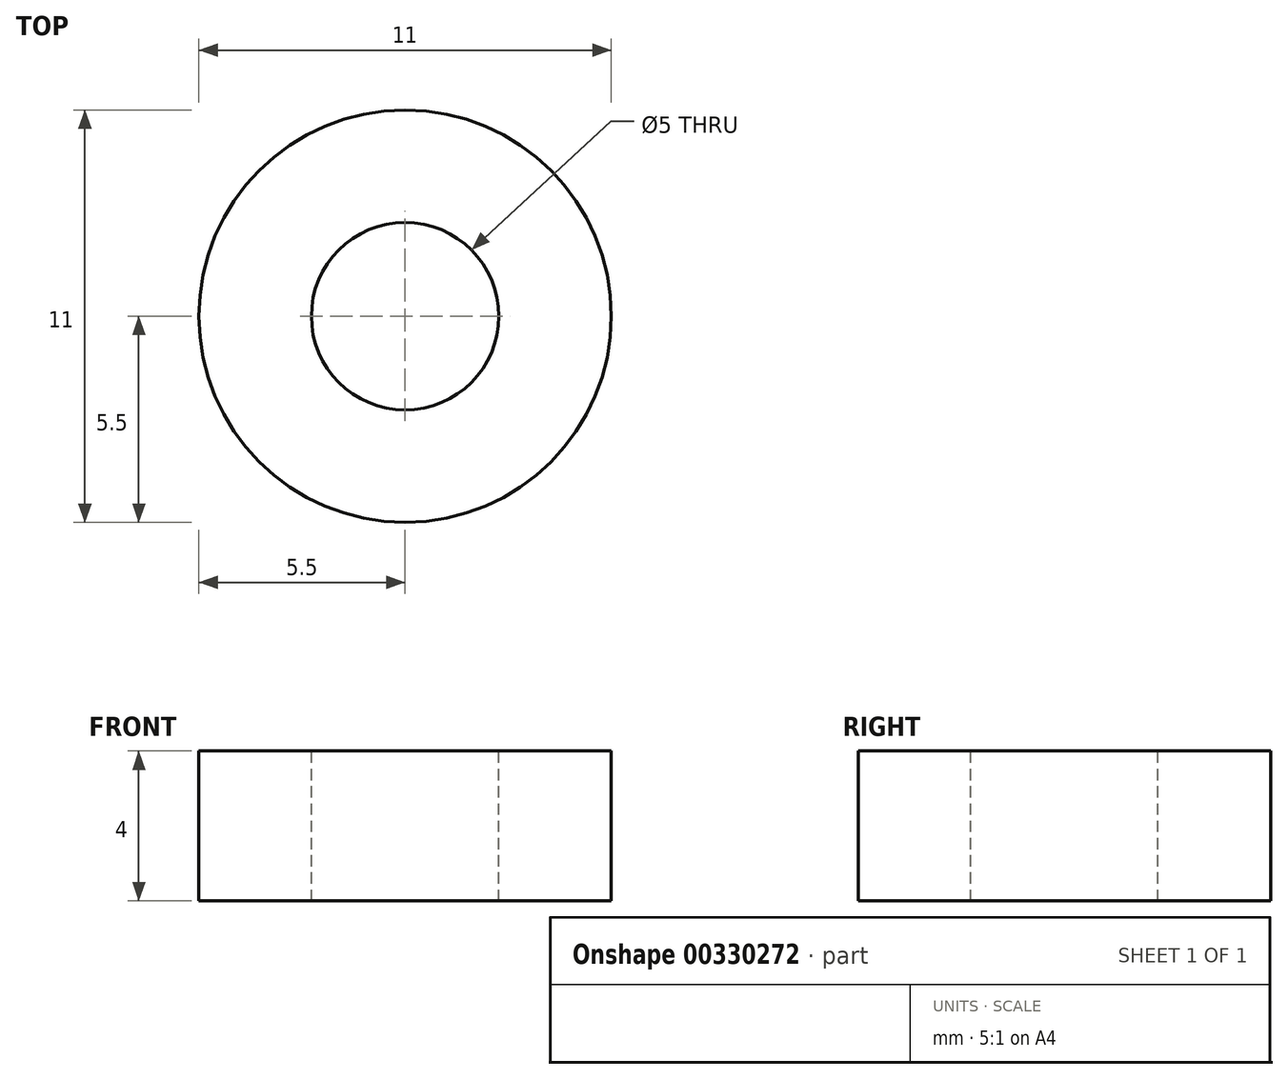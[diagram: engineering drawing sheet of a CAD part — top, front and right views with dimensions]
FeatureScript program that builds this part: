
annotation { "Feature Type Name" : "Feature", "Feature Type Description" : "" }
export const myFeature = defineFeature(function(context is Context, id is Id, definition is map)
    precondition{}
    {
        {
            var Q0;
            Q0=qCreatedBy(makeId("Top.planeOp"),FACE);
            var sketch = newSketch(context, id + "F0", { "sketchPlane" : qUnion([Q0])});
            skCircle(sketch, "E0", {"center": v(0, 0) * mm, "radius": 5.5 * mm});
            skSolve(sketch);
        }
        {
            var Q0;
            Q0 = qSketchRegion(id + "F0", true);
            extrude(context, id + "F1", {"entities" : qUnion([Q0]), "depth" : 4 * mm});
        }
        {
            var Q0;
            Q0=makeQuery(id+"F1.opExtrude","CAP_FACE",FACE,{"disambiguationData":[OSD([sQuery(id+"F0.wireOp",EDGE,"E0")])],"isStart":false});
            var sketch = newSketch(context, id + "F2", { "sketchPlane" : qUnion([Q0])});
            skCircle(sketch, "E1", {"center": v(0, 0) * mm, "radius": 2.5 * mm});
            skSolve(sketch);
        }
        {
            var Q0;
            Q0=sQuery(id+"F2.wireOp",VERTEX,"E1.center");
            var Q1;
            Q1=makeQuery(id+"F1.opExtrude","SWEPT_BODY",BODY,{"disambiguationData":[OSD([sQuery(id+"F0.wireOp",EDGE,"E0")])]});
            hole(context, id + "F3", {"style" : HoleStyle.SIMPLE, "endStyle" : HoleEndStyle.THROUGH, "holeDiameter" : 5 * mm, "tappedDepth" : 12 * mm, "tapClearance" : 3, "locations" : qUnion([Q0]), "scope" : qUnion([Q1])});
        }
    });
